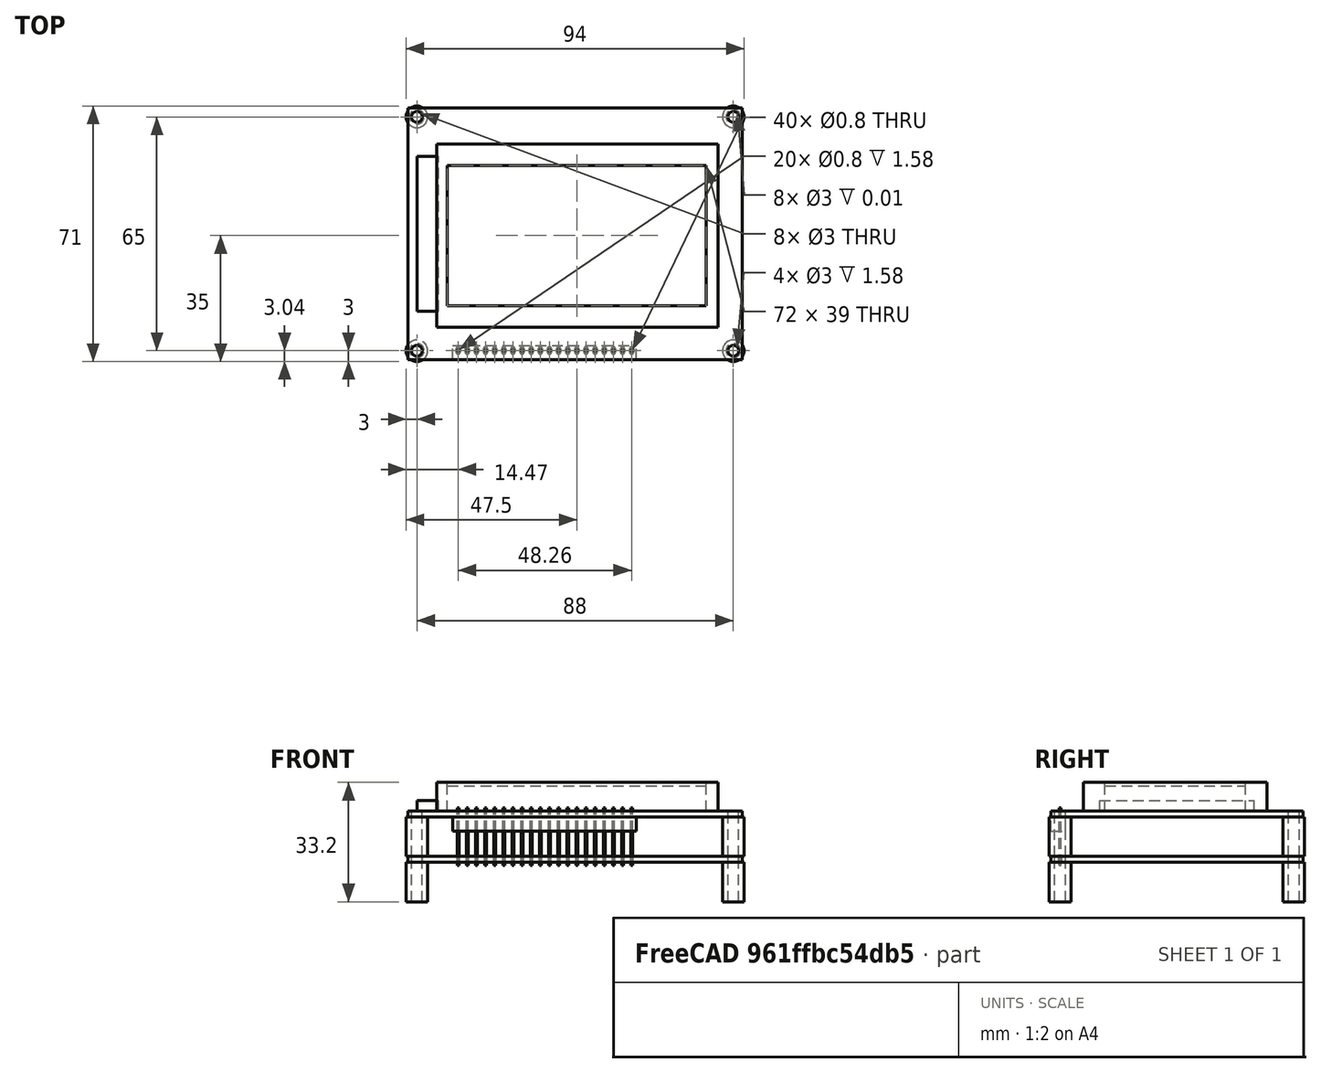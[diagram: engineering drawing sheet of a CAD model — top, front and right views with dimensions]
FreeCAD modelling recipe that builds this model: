
FCSTD DOCUMENT  (FreeCAD 0.18R16146 (Git))
Label: glcd
License: All rights reserved
LicenseURL: http://en.wikipedia.org/wiki/All_rights_reserved
objects: Part::Box×22, Part::Cylinder×12, Part::MultiFuse×9, Part::Feature×8, Part::FeaturePython×5, App::DocumentObjectGroup×1
note: 56 computed .brp shape members not serialized (recipe doc carries the construction recipe); baked Part::Feature solids carry a one-line shape summary decoded from their .brp

FEATURE [Part::FeaturePython] FCrtYd_lines  label="FCrtYd"  # a2plus imported part (geometry in sourceFile) (typed FeaturePython)
  fixedPosition = true
FEATURE [Part::FeaturePython] Filk_lines  label="FrontSilk"  # a2plus imported part (geometry in sourceFile) (typed FeaturePython)
  fixedPosition = true
FEATURE [Part::FeaturePython] TopPads  # a2plus imported part (geometry in sourceFile) (typed FeaturePython)
  fixedPosition = true
FEATURE [Part::FeaturePython] BotPads  # a2plus imported part (geometry in sourceFile) (typed FeaturePython)
  fixedPosition = true
FEATURE [Part::FeaturePython] THPs  label="PTHs"  # a2plus imported part (geometry in sourceFile) (typed FeaturePython)
  fixedPosition = true
FEATURE [App::DocumentObjectGroup] _2864B_fp
  Group = -> [FCrtYd_lines,Filk_lines,TopPads,BotPads,THPs]
FEATURE [Part::Box] Box  label="Würfel"
  AttacherType = Attacher::AttachEngine3D
  Height = 1.6
  Length = 93
  Placement = pos=(0,0,-1.6) rot=(0,0,1;0rad)
  Width = 70
FEATURE [Part::Cylinder] Cylinder  label="Zylinder"
  Angle = 360
  AttacherType = Attacher::AttachEngine3D
  Height = 11
  Placement = pos=(2.5,2.5,0) rot=(0,0,1;0rad)
  Radius = 3
FEATURE [Part::Cylinder] Cylinder001  label="Zylinder001"
  Angle = 360
  AttacherType = Attacher::AttachEngine3D
  Height = 11
  Placement = pos=(2.5,2.5,0) rot=(0,0,1;0rad)
  Radius = 1.5
FEATURE [Part::Cylinder] Cylinder002  label="Zylinder002"
  Angle = 360
  AttacherType = Attacher::AttachEngine3D
  Height = 11
  Placement = pos=(90.5,2.5,0) rot=(0,0,1;0rad)
  Radius = 3
FEATURE [Part::Cylinder] Cylinder003  label="Zylinder003"
  Angle = 360
  AttacherType = Attacher::AttachEngine3D
  Height = 11
  Placement = pos=(90.5,2.5,0) rot=(0,0,1;0rad)
  Radius = 1.5
FEATURE [Part::Cylinder] Cylinder004  label="Zylinder004"
  Angle = 360
  AttacherType = Attacher::AttachEngine3D
  Height = 11
  Placement = pos=(90.5,67.5,0) rot=(0,0,1;0rad)
  Radius = 3
FEATURE [Part::Cylinder] Cylinder005  label="Zylinder005"
  Angle = 360
  AttacherType = Attacher::AttachEngine3D
  Height = 11
  Placement = pos=(90.5,67.5,0) rot=(0,0,1;0rad)
  Radius = 1.5
FEATURE [Part::Cylinder] Cylinder006  label="Zylinder006"
  Angle = 360
  AttacherType = Attacher::AttachEngine3D
  Height = 11
  Placement = pos=(2.5,67.5,0) rot=(0,0,1;0rad)
  Radius = 3
FEATURE [Part::Cylinder] Cylinder007  label="Zylinder007"
  Angle = 360
  AttacherType = Attacher::AttachEngine3D
  Height = 11
  Placement = pos=(2.5,67.5,0) rot=(0,0,1;0rad)
  Radius = 1.5
FEATURE [Part::MultiFuse] Fusion
  Placement = pos=(0,0,-12.6) rot=(0,0,1;0rad)
  Shapes = -> [Cylinder002,Cylinder,Cylinder004,Cylinder006]
FEATURE [Part::Cylinder] Cylinder008  label="Zylinder008"
  Angle = 360
  AttacherType = Attacher::AttachEngine3D
  Height = 1.6
  Placement = pos=(2.5,2.5,0) rot=(0,0,1;0rad)
  Radius = 1.5
FEATURE [Part::Cylinder] Cylinder009  label="Zylinder009"
  Angle = 360
  AttacherType = Attacher::AttachEngine3D
  Height = 1.6
  Placement = pos=(90.5,2.5,0) rot=(0,0,1;0rad)
  Radius = 1.5
FEATURE [Part::Cylinder] Cylinder010  label="Zylinder010"
  Angle = 360
  AttacherType = Attacher::AttachEngine3D
  Height = 1.6
  Placement = pos=(90.5,67.5,0) rot=(0,0,1;0rad)
  Radius = 1.5
FEATURE [Part::Cylinder] Cylinder011  label="Zylinder011"
  Angle = 360
  AttacherType = Attacher::AttachEngine3D
  Height = 1.6
  Placement = pos=(2.5,67.5,0) rot=(0,0,1;0rad)
  Radius = 1.5
FEATURE [Part::MultiFuse] Fusion001
  Placement = pos=(0,0,-12.6) rot=(0,0,1;0rad)
  Shapes = -> [Cylinder001,Cylinder003,Cylinder005,Cylinder007]
FEATURE [Part::MultiFuse] Fusion002
  Placement = pos=(0,0,-1.6) rot=(0,0,1;0rad)
  Shapes = -> [Cylinder011,Cylinder009,Cylinder010,Cylinder008]
FEATURE [Part::Feature] Shape001  label="base"
  Placement = pos=(0,0,12.6) rot=(0,0,1;0rad)
  shape: bbox 78.3 x 51 x 8 mm, 6 faces (baked)
FEATURE [Part::Box] Box001  label="Würfel001"
  AttacherType = Attacher::AttachEngine3D
  Height = 8
  Length = 72
  Placement = pos=(11,15,12.6) rot=(0,0,1;0rad)
  Width = 39
FEATURE [Part::Box] Box004  label="Würfel002"
  AttacherType = Attacher::AttachEngine3D
  Height = 16
  Length = 0.5
  Placement = pos=(13.7,2.28,-2.5) rot=(0,0,1;0rad)
  Width = 0.5
FEATURE [Part::Box] Box005  label="Würfel003"
  AttacherType = Attacher::AttachEngine3D
  Height = 16
  Length = 0.5
  Placement = pos=(16.24,2.28,-2.5) rot=(0,0,1;0rad)
  Width = 0.5
FEATURE [Part::Box] Box006  label="Würfel004"
  AttacherType = Attacher::AttachEngine3D
  Height = 16
  Length = 0.5
  Placement = pos=(18.78,2.28,-2.5) rot=(0,0,1;0rad)
  Width = 0.5
FEATURE [Part::Box] Box007  label="Würfel005"
  AttacherType = Attacher::AttachEngine3D
  Height = 16
  Length = 0.5
  Placement = pos=(21.32,2.28,-2.5) rot=(0,0,1;0rad)
  Width = 0.5
FEATURE [Part::Box] Box008  label="Würfel006"
  AttacherType = Attacher::AttachEngine3D
  Height = 16
  Length = 0.5
  Placement = pos=(23.86,2.28,-2.5) rot=(0,0,1;0rad)
  Width = 0.5
FEATURE [Part::MultiFuse] Fusion003
  Shapes = -> [Box004,Box006,Box007,Box008,Box005]
FEATURE [Part::Box] Box009  label="Würfel007"
  AttacherType = Attacher::AttachEngine3D
  Height = 16
  Length = 0.5
  Placement = pos=(18.78,2.28,-2.5) rot=(0,0,1;0rad)
  Width = 0.5
FEATURE [Part::Box] Box010  label="Würfel008"
  AttacherType = Attacher::AttachEngine3D
  Height = 16
  Length = 0.5
  Placement = pos=(21.32,2.28,-2.5) rot=(0,0,1;0rad)
  Width = 0.5
FEATURE [Part::Box] Box011  label="Würfel009"
  AttacherType = Attacher::AttachEngine3D
  Height = 16
  Length = 0.5
  Placement = pos=(13.7,2.28,-2.5) rot=(0,0,1;0rad)
  Width = 0.5
FEATURE [Part::Box] Box012  label="Würfel010"
  AttacherType = Attacher::AttachEngine3D
  Height = 16
  Length = 0.5
  Placement = pos=(23.86,2.28,-2.5) rot=(0,0,1;0rad)
  Width = 0.5
FEATURE [Part::Box] Box013  label="Würfel011"
  AttacherType = Attacher::AttachEngine3D
  Height = 16
  Length = 0.5
  Placement = pos=(16.24,2.28,-2.5) rot=(0,0,1;0rad)
  Width = 0.5
FEATURE [Part::MultiFuse] Fusion004
  Placement = pos=(12.7,0,0) rot=(0,0,1;0rad)
  Shapes = -> [Box011,Box009,Box010,Box012,Box013]
FEATURE [Part::MultiFuse] Fusion005
  Shapes = -> [Fusion003,Fusion004]
FEATURE [Part::Box] Box014  label="Würfel012"
  AttacherType = Attacher::AttachEngine3D
  Height = 16
  Length = 0.5
  Placement = pos=(18.78,2.28,-2.5) rot=(0,0,1;0rad)
  Width = 0.5
FEATURE [Part::Box] Box015  label="Würfel013"
  AttacherType = Attacher::AttachEngine3D
  Height = 16
  Length = 0.5
  Placement = pos=(21.32,2.28,-2.5) rot=(0,0,1;0rad)
  Width = 0.5
FEATURE [Part::Box] Box016  label="Würfel014"
  AttacherType = Attacher::AttachEngine3D
  Height = 16
  Length = 0.5
  Placement = pos=(13.7,2.28,-2.5) rot=(0,0,1;0rad)
  Width = 0.5
FEATURE [Part::Box] Box017  label="Würfel015"
  AttacherType = Attacher::AttachEngine3D
  Height = 16
  Length = 0.5
  Placement = pos=(13.7,2.28,-2.5) rot=(0,0,1;0rad)
  Width = 0.5
FEATURE [Part::Box] Box018  label="Würfel016"
  AttacherType = Attacher::AttachEngine3D
  Height = 16
  Length = 0.5
  Placement = pos=(23.86,2.28,-2.5) rot=(0,0,1;0rad)
  Width = 0.5
FEATURE [Part::Box] Box019  label="Würfel017"
  AttacherType = Attacher::AttachEngine3D
  Height = 16
  Length = 0.5
  Placement = pos=(21.32,2.28,-2.5) rot=(0,0,1;0rad)
  Width = 0.5
FEATURE [Part::Box] Box020  label="Würfel018"
  AttacherType = Attacher::AttachEngine3D
  Height = 16
  Length = 0.5
  Placement = pos=(16.24,2.28,-2.5) rot=(0,0,1;0rad)
  Width = 0.5
FEATURE [Part::Box] Box021  label="Würfel019"
  AttacherType = Attacher::AttachEngine3D
  Height = 16
  Length = 0.5
  Placement = pos=(16.24,2.28,-2.5) rot=(0,0,1;0rad)
  Width = 0.5
FEATURE [Part::Box] Box022  label="Würfel020"
  AttacherType = Attacher::AttachEngine3D
  Height = 16
  Length = 0.5
  Placement = pos=(18.78,2.28,-2.5) rot=(0,0,1;0rad)
  Width = 0.5
FEATURE [Part::MultiFuse] Fusion008
  Shapes = -> [Box016,Box014,Box015,Box018,Box020]
FEATURE [Part::Box] Box023  label="Würfel021"
  AttacherType = Attacher::AttachEngine3D
  Height = 16
  Length = 0.5
  Placement = pos=(23.86,2.28,-2.5) rot=(0,0,1;0rad)
  Width = 0.5
FEATURE [Part::MultiFuse] Fusion006
  Placement = pos=(12.7,0,0) rot=(0,0,1;0rad)
  Shapes = -> [Box017,Box022,Box019,Box023,Box021]
FEATURE [Part::MultiFuse] Fusion007
  Placement = pos=(25.4,0,0) rot=(0,0,1;0rad)
  Shapes = -> [Fusion008,Fusion006]
FEATURE [Part::Feature] Shape  label="led"
  shape: bbox 6 x 43 x 3 mm, 6 faces (baked)
FEATURE [Part::Feature] Shape005  label="stand"
  shape: bbox 94 x 71 x 11 mm, 16 faces, 4 solids (baked)
FEATURE [Part::Feature] Shape006  label="pins"
  shape: bbox 48.76 x 0.5 x 16 mm, 120 faces, 20 solids (baked)
FEATURE [Part::Feature] Shape007  label="header"
  shape: bbox 51 x 4 x 4 mm, 6 faces (baked)
FEATURE [Part::Feature] Shape008  label="frame"
  shape: bbox 78.3 x 51 x 8 mm, 10 faces (baked)
FEATURE [Part::Feature] Shape009  label="display"
  shape: bbox 72 x 39 x 7 mm, 6 faces (baked)
FEATURE [Part::Feature] Shape010  label="pcb"
  shape: bbox 93 x 70 x 1.6 mm, 10 faces (baked)
